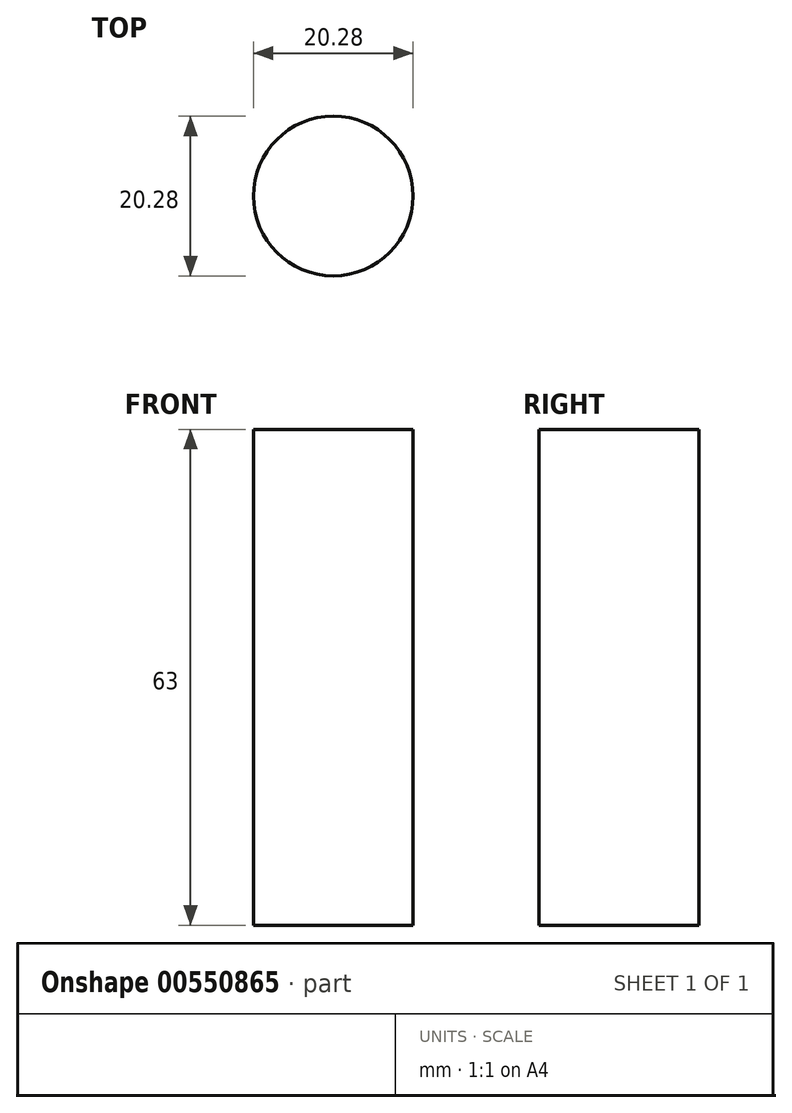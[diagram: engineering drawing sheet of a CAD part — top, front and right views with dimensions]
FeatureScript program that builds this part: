
annotation { "Feature Type Name" : "Feature", "Feature Type Description" : "" }
export const myFeature = defineFeature(function(context is Context, id is Id, definition is map)
    precondition{}
    {
        {
            var Q0;
            Q0=qCreatedBy(makeId("Top.planeOp"),FACE);
            var sketch = newSketch(context, id + "F0", { "sketchPlane" : qUnion([Q0])});
            skCircle(sketch, "E0", {"center": v(0, 0) * mm, "radius": 10.14 * mm});
            skSolve(sketch);
        }
        {
            var Q0;
            Q0 = qSketchRegion(id + "F0", true);
            extrude(context, id + "F1", {"entities" : qUnion([Q0]), "depth" : 25.4 * mm, "offsetDistance" : 25.4 * mm});
        }
        {
            var Q0;
            Q0 = qSketchRegion(id + "F0", true);
            var Q1;
            Q1=makeQuery(id+"F1.opExtrude","CAP_FACE",FACE,{"disambiguationData":[OSD([sQuery(id+"F0.wireOp",EDGE,"E0")])],"isStart":false});
            var Q2;
            Q2 = qSketchRegion(id + "FgeMIi3UMMAOhnY_0", true);
            extrude(context, id + "F2", {"entities" : qUnion([Q0, Q1, Q2]), "operationType" : NewBodyOperationType.ADD, "oppositeDirection" : true, "depth" : 37.6 * mm, "offsetDistance" : 25.4 * mm});
        }
    });
